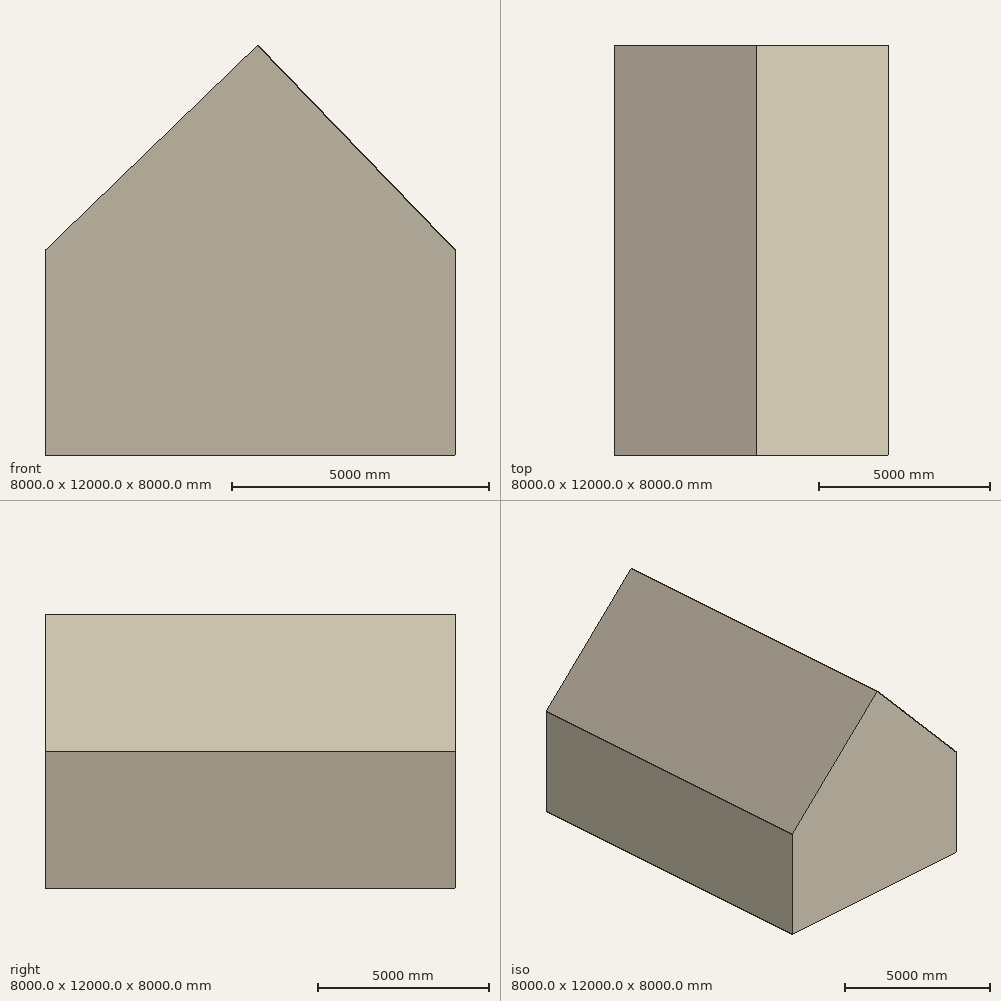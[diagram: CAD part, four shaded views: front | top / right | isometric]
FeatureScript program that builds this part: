
annotation { "Feature Type Name" : "Feature", "Feature Type Description" : "" }
export const myFeature = defineFeature(function(context is Context, id is Id, definition is map)
    precondition{}
    {
        {
            var Q0;
            Q0=qCreatedBy(makeId("Front.planeOp"),FACE);
            var sketch = newSketch(context, id + "F0", { "sketchPlane" : qUnion([Q0])});
            skLineSegment(sketch, "E0.bottom", {"start": v(0, 0) * mm, "end": v(8000, 0) * mm});
            skLineSegment(sketch, "E0.top", {"start": v(0, -4000) * mm, "end": v(8000, -4000) * mm});
            skLineSegment(sketch, "E0.left", {"start": v(0, 0) * mm, "end": v(0, -4000) * mm});
            skLineSegment(sketch, "E0.right", {"start": v(8000, 0) * mm, "end": v(8000, -4000) * mm});
            skLineSegment(sketch, "E1", {"start": v(8000, 0) * mm, "end": v(4144.98, 4000) * mm});
            skLineSegment(sketch, "E2", {"start": v(4144.98, 4000) * mm, "end": v(0, 0) * mm});
            skSolve(sketch);
        }
        {
            var Q0;
            Q0 = qSketchRegion(id + "F0", true);
            extrude(context, id + "F1", {"entities" : qUnion([Q0]), "depth" : 12000 * mm});
        }
    });
